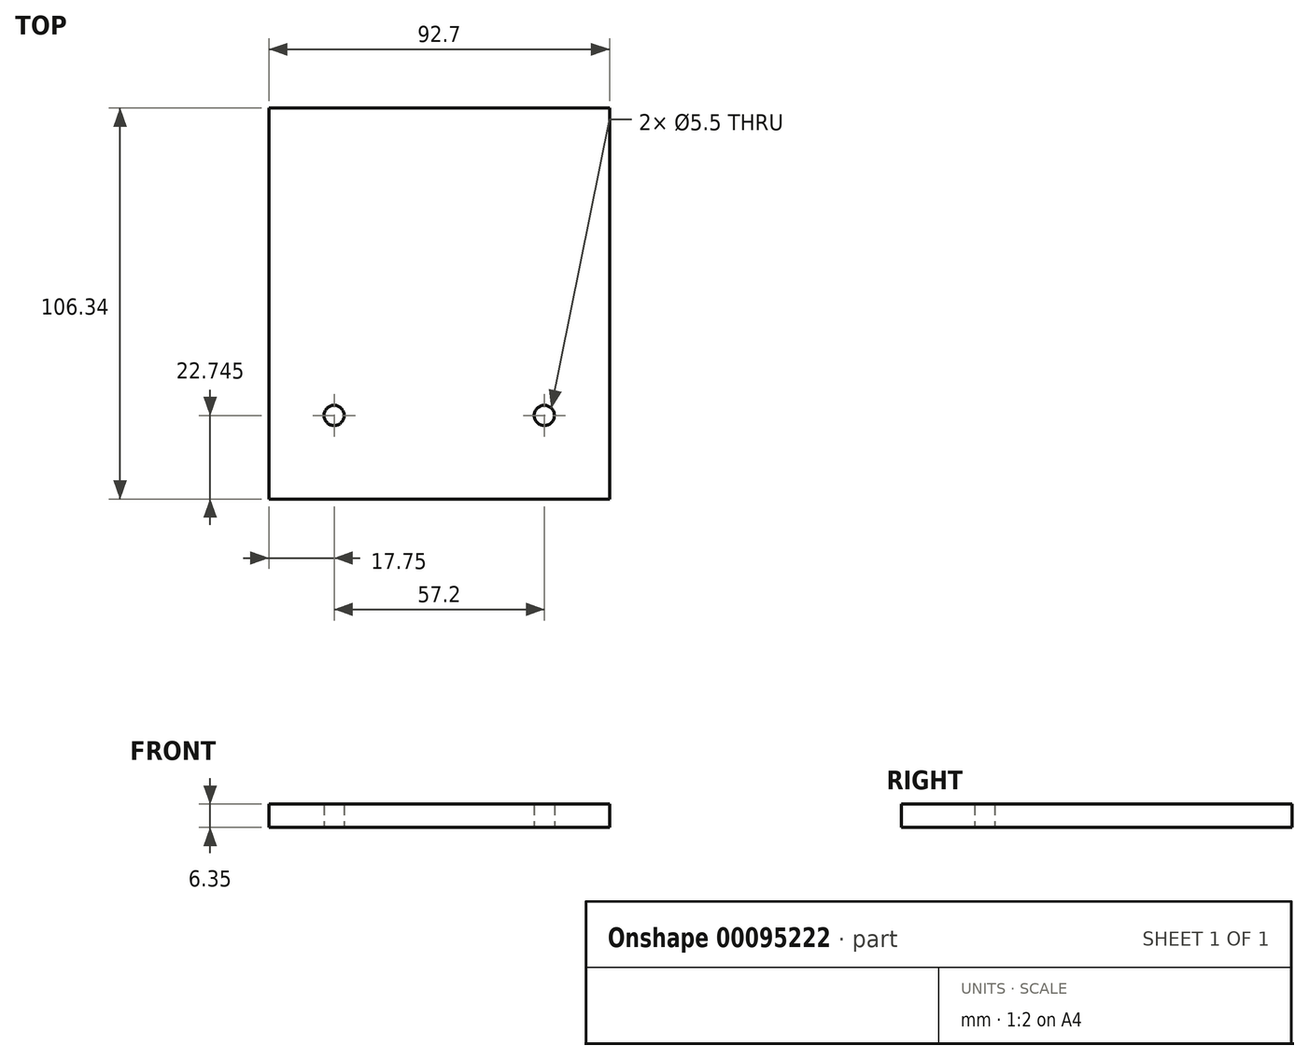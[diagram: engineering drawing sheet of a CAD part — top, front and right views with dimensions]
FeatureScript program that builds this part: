
annotation { "Feature Type Name" : "Feature", "Feature Type Description" : "" }
export const myFeature = defineFeature(function(context is Context, id is Id, definition is map)
    precondition{}
    {
        {
            var Q0;
            Q0=qCreatedBy(makeId("Top.planeOp"),FACE);
            var sketch = newSketch(context, id + "F0", { "sketchPlane" : qUnion([Q0])});
            skLineSegment(sketch, "E0.bottom", {"start": v(46.35, 53.17) * mm, "end": v(-46.35, 53.17) * mm});
            skLineSegment(sketch, "E0.top", {"start": v(46.35, -53.17) * mm, "end": v(-46.35, -53.17) * mm});
            skLineSegment(sketch, "E0.left", {"start": v(46.35, 53.17) * mm, "end": v(46.35, -53.17) * mm});
            skLineSegment(sketch, "E0.right", {"start": v(-46.35, 53.17) * mm, "end": v(-46.35, -53.17) * mm});
            skPoint(sketch, "E0.middle", {"position": v(0, 0) * mm});
            skCircle(sketch, "E1", {"center": v(28.6, -30.42) * mm, "radius": 2.75 * mm});
            skLineSegment(sketch, "E2", {"start": v(28.6, -33.17) * mm, "end": v(28.6, -53.17) * mm, "construction": true});
            skLineSegment(sketch, "E3", {"start": v(31.35, -30.42) * mm, "end": v(46.35, -30.42) * mm, "construction": true});
            skLineSegment(sketch, "E4", {"start": v(28.6, -33.17) * mm, "end": v(28.6, -30.42) * mm, "construction": true});
            skLineSegment(sketch, "E5", {"start": v(31.35, -30.42) * mm, "end": v(28.6, -30.42) * mm, "construction": true});
            skCircle(sketch, "E6.MirrorC", {"center": v(-28.6, -30.42) * mm, "radius": 2.75 * mm});
            skSolve(sketch);
        }
        {
            var Q0;
            Q0=makeQuery(id+"F0.imprint","IMPRINT",FACE,{"disambiguationData":[TD([[makeQuery(id+"F0.imprint","IMPRINT",EDGE,{"derivedFrom":sQuery(id+"F0.wireOp",EDGE,"E0.bottom")}),1.0]])]});
            extrude(context, id + "F1", {"entities" : qUnion([Q0]), "depth" : 6.35 * mm});
        }
    });
